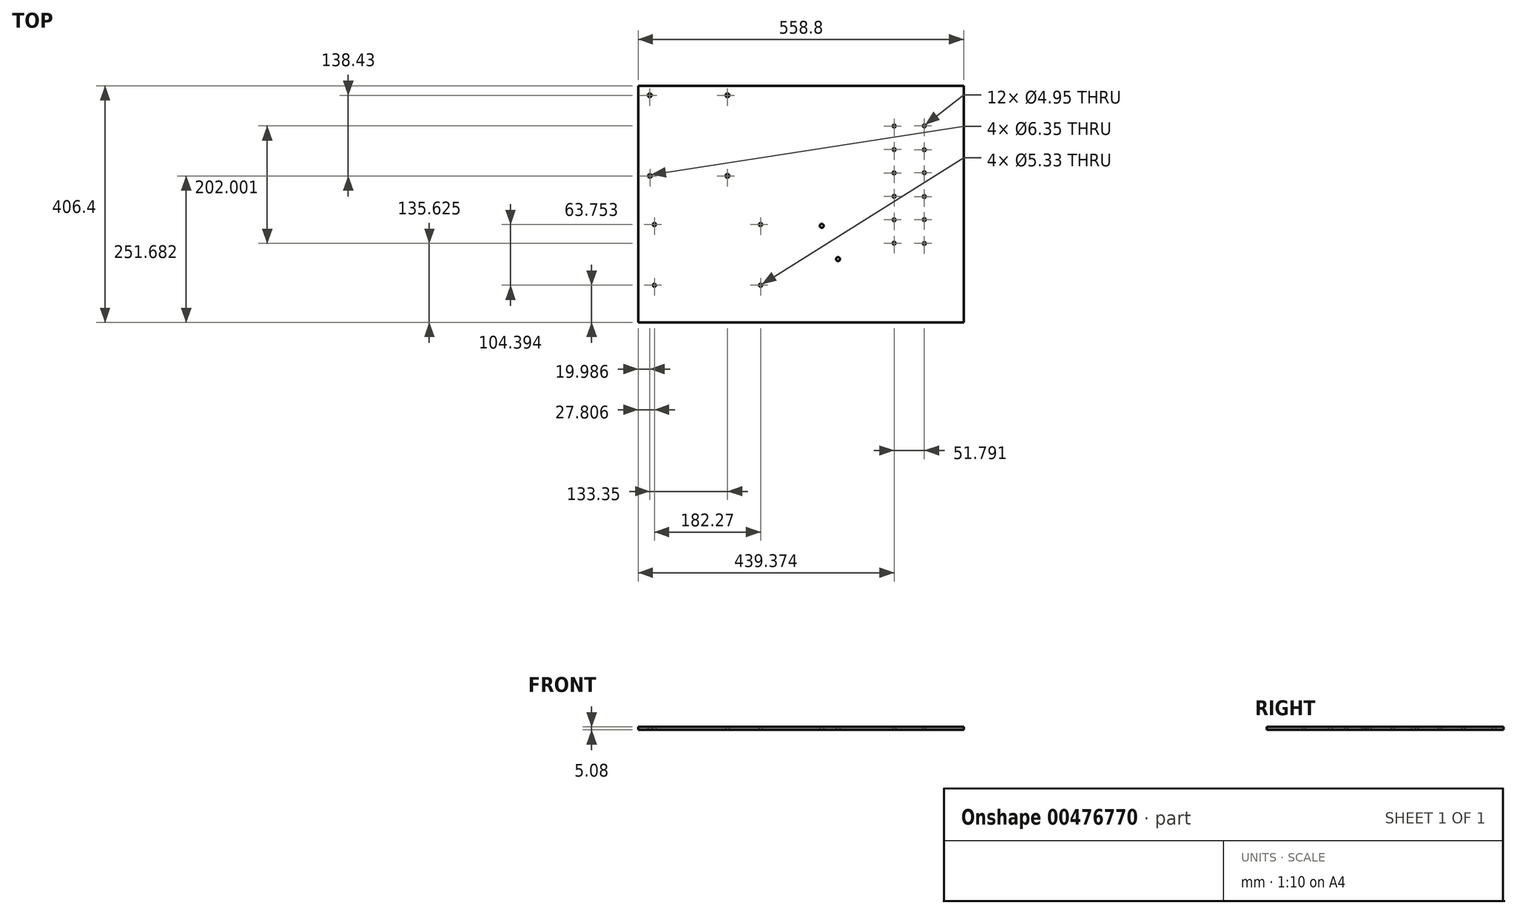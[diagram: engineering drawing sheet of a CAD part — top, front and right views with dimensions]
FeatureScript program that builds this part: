
annotation { "Feature Type Name" : "Feature", "Feature Type Description" : "" }
export const myFeature = defineFeature(function(context is Context, id is Id, definition is map)
    precondition{}
    {
        {
            var Q0;
            Q0=qCreatedBy(makeId("Top.planeOp"),FACE);
            var sketch = newSketch(context, id + "F0", { "sketchPlane" : qUnion([Q0])});
            skLineSegment(sketch, "E0.bottom", {"start": v(-59.86, 570.58) * mm, "end": v(498.94, 570.58) * mm});
            skLineSegment(sketch, "E0.top", {"start": v(-59.86, 164.18) * mm, "end": v(498.94, 164.18) * mm});
            skLineSegment(sketch, "E0.left", {"start": v(-59.86, 570.58) * mm, "end": v(-59.86, 164.18) * mm});
            skLineSegment(sketch, "E0.right", {"start": v(498.94, 570.58) * mm, "end": v(498.94, 164.18) * mm});
            skCircle(sketch, "E1", {"center": v(-39.87, 554.3) * mm, "radius": 3.18 * mm});
            skCircle(sketch, "E2", {"center": v(379.51, 380.68) * mm, "radius": 2.48 * mm});
            skLineSegment(sketch, "E3", {"start": v(379.51, 380.68) * mm, "end": v(382, 380.68) * mm, "construction": true});
            skCircle(sketch, "E4.MirrorC", {"center": v(431.3, 380.3) * mm, "radius": 2.48 * mm});
            skCircle(sketch, "E5.MirrorC", {"center": v(379.51, 340.44) * mm, "radius": 2.48 * mm});
            skCircle(sketch, "E6.MirrorC", {"center": v(431.3, 340.82) * mm, "radius": 2.48 * mm});
            skCircle(sketch, "E7.MirrorC", {"center": v(379.51, 300.2) * mm, "radius": 2.48 * mm});
            skCircle(sketch, "E8.MirrorC", {"center": v(431.3, 299.8) * mm, "radius": 2.48 * mm});
            skCircle(sketch, "E9.MirrorC", {"center": v(379.51, 420.93) * mm, "radius": 2.48 * mm});
            skCircle(sketch, "E10.MirrorC", {"center": v(431.3, 421.31) * mm, "radius": 2.48 * mm});
            skCircle(sketch, "E11.MirrorC", {"center": v(379.51, 461.18) * mm, "radius": 2.48 * mm});
            skCircle(sketch, "E12.MirrorC", {"center": v(431.3, 460.8) * mm, "radius": 2.48 * mm});
            skCircle(sketch, "E13.MirrorC", {"center": v(379.51, 501.42) * mm, "radius": 2.48 * mm});
            skCircle(sketch, "E14.MirrorC", {"center": v(431.3, 501.8) * mm, "radius": 2.48 * mm});
            skCircle(sketch, "E15", {"center": v(93.48, 554.3) * mm, "radius": 3.18 * mm});
            skCircle(sketch, "E16", {"center": v(-39.67, 415.86) * mm, "radius": 3.18 * mm});
            skCircle(sketch, "E17", {"center": v(93.48, 415.86) * mm, "radius": 3.18 * mm});
            skCircle(sketch, "E18", {"center": v(-32.05, 227.93) * mm, "radius": 2.67 * mm});
            skCircle(sketch, "E19", {"center": v(150.22, 227.93) * mm, "radius": 2.67 * mm});
            skCircle(sketch, "E20", {"center": v(-32.05, 332.33) * mm, "radius": 2.67 * mm});
            skCircle(sketch, "E21", {"center": v(150.22, 332.33) * mm, "radius": 2.67 * mm});
            skCircle(sketch, "E22", {"center": v(255.24, 330.03) * mm, "radius": 3.43 * mm});
            skLineSegment(sketch, "E23", {"start": v(255.24, 330.03) * mm, "end": v(255.24, 272.88) * mm, "construction": true});
            skCircle(sketch, "E24", {"center": v(283.18, 272.88) * mm, "radius": 3.43 * mm});
            skSolve(sketch);
        }
        {
            var Q0;
            Q0=makeQuery(id+"F0.imprint","IMPRINT",FACE,{"disambiguationData":[TD([[makeQuery(id+"F0.imprint","IMPRINT",EDGE,{"derivedFrom":sQuery(id+"F0.wireOp",EDGE,"E0.bottom")}),-1.0]])]});
            extrude(context, id + "F1", {"entities" : qUnion([Q0]), "depth" : 5.08 * mm});
        }
    });
